# Revit family: Building-ConnessioniIEC309-GEWISS-67IB-PRESE-INTERBLOCCATE_IP67_SENZA_FONDO_63A_FUS
name_source: partatom
category: Apparecchi elettrici
units: mm (PartAtom-declared; Revit-internal decimal feet)

## family parameters
Condiviso = Sì
Host = Superficie
Mantenere orientamento annotazione = Sì
Punto di calcolo locali = Sì
Quota connettore circolare = Usa diametro
Taglio con vuoti quando caricato = Sì
Tipo di parte = Normale

## types (11) — shared parameters
Catalogo = BUILDING
Catalogo Serie = 67 IB
Codice Electrocod = 2222
Con fondo = No
Corpo presa = GEWISS -BLU
Corrente nominale (A) = 63
Corrente nominale (In) = 63
Corrente nominale di cortocircuito (Icc) = 10KA
Frequenza = 50/60 Hz
Frequenza nominale (Hz) = 50/60 Hz
Glow Wire Test = 850 °C
Glow wire test: = 850 °C
Grado di protezione = IP67
IDF = 4c4d9059-d908-47b0-b065-80ef8b62f6a7
IDT = 4db8474b-84e3-4347-92c1-42259bd8bc9a
Immagine tipo = H.jpg
Peso = Max. 2,2 Kg
Peso (kg) = Max. 2,2 Kg
Potere di interruzione fusibili = > 50 kA
Produttore = GEWISS S.p.A.
Prospetto di default = 1219 mm
Protezione = Base portafusibile (CBF)
Resistenza agli urti = IK08
SEO = Presa
Scheda Tecnica = https://www.gewiss.com
Simbolo presa = PRESAINDSTAGNA : 3P
Struttura = Grigio RAL - 7035
Temperatura di funzionamento = -25 ÷ +40 °C
Temperatura di utilizzo = -25 +40 °C
Tensione nominale di isolamento (Ui) = 500V
Tensione nominale di tenuta ad impulso = 4KV
Termopressione con biglia = 125 °C
Tipo fusibile = Ã˜ 22x58 mm
Tipologia = Verticale
URL = https://www.gewiss.com
Versione file RFA = 21.4
presa = rosso
zero-valued in all types: giallo

## per-type parameters (varying)
| type | Codice EAN | Colore | Colore: | Corrente nominale (In) presa IB | Descrizione | Modello | N. poli | Numero di poli | Riferimento h | Tensione nominale | Tensione nominale: |
| GW66352N - PR.BL IP67 S.F.3P+T 63A 400V 6H CBF | 8011564742079 | Rosso | Rosso | 52A | PR.BL IP67 S.F.3P+T 63A 400V 6H CBF | GW66352N | 3P+T | 3P+T | 6 | 380 - 415 V | 380 - 415 V |
| GW66347N - PR.BL IP67 S.F.3P+N+T 63A 110V 4H CBF | 8011564742024 | Giallo | Giallo | 48A | PR.BL IP67 S.F.3P+N+T 63A 110V 4H CBF | GW66347N | 3P+N+T | 3P+N+T | 4 | 100 - 130 V | 100 - 130 V |
| GW66351N - PR.BL IP67 S.F.2P+T 63A 400V 9H CBF | 8011564742062 | Rosso | Rosso | 54A | PR.BL IP67 S.F.2P+T 63A 400V 9H CBF | GW66351N | 2P+T | 2P+T | 9 | 380 - 415 V | 380 - 415 V |
| GW66350N - PR.BL IP67 S.F.3P+N+T 63A 230V 9H CBF | 8011564742055 | Blu | Blu | 48A | PR.BL IP67 S.F.3P+N+T 63A 230V 9H CBF | GW66350N | 3P+N+T | 3P+N+T | 9 | 200 - 250 V | 200 - 250 V |
| GW66353N - PR.BL IP67 S.F.3P+N+T 63A 400V 6H CBF | 8011564742086 | Rosso | Rosso | 48A | PR.BL IP67 S.F.3P+N+T 63A 400V 6H CBF | GW66353N | 3P+N+T | 3P+N+T | 6 | 380 - 415 V | 380 - 415 V |
| GW66354N - PR.BL IP67 S.F.3P+T 63A 500V 7H CBF | 8011564742093 | Nero | Nero | 52A | PR.BL IP67 S.F.3P+T 63A 500V 7H CBF | GW66354N | 3P+T | 3P+T | 7 | 480 - 500 V | 480 - 500 V |
| GW66349N - PR.BL IP67 S.F.3P+T 63A 230V 9H CBF | 8011564742048 | Blu | Blu | 52A | PR.BL IP67 S.F.3P+T 63A 230V 9H CBF | GW66349N | 3P+T | 3P+T | 9 | 200 - 250 V | 200 - 250 V |
| GW66355N - PR.BL IP67 S.F.3P+N+T 63A 500V 7H CBF | 8011564742109 | Nero | Nero | 48A | PR.BL IP67 S.F.3P+N+T 63A 500V 7H CBF | GW66355N | 3P+N+T | 3P+N+T | 7 | 480 - 500 V | 480 - 500 V |
| GW66348N - PR.BL IP67 S.F.2P+T 63A 230V 6H CBF | 8011564742031 | Blu | Blu | 54A | PR.BL IP67 S.F.2P+T 63A 230V 6H CBF | GW66348N | 2P+T | 2P+T | 6 | 200 - 250 V | 200 - 250 V |
| GW66346N - PR.BL IP67 S.F.3P+T 63A 110V 4H CBF | 8011564742017 | Giallo | Giallo | 52A | PR.BL IP67 S.F.3P+T 63A 110V 4H CBF | GW66346N | 3P+T | 3P+T | 4 | 100 - 130 V | 100 - 130 V |
| GW66345N - PR.BL IP67 S.F.2P+T 63A 110V 4H CBF | 8011564742000 | Giallo | Giallo | 54A | PR.BL IP67 S.F.2P+T 63A 110V 4H CBF | GW66345N | 2P+T | 2P+T | 4 | 100 - 130 V | 100 - 130 V |

## geometry (parser evidence)
native form markers: Sweep x5
no freeform markers — native parametric forms only
